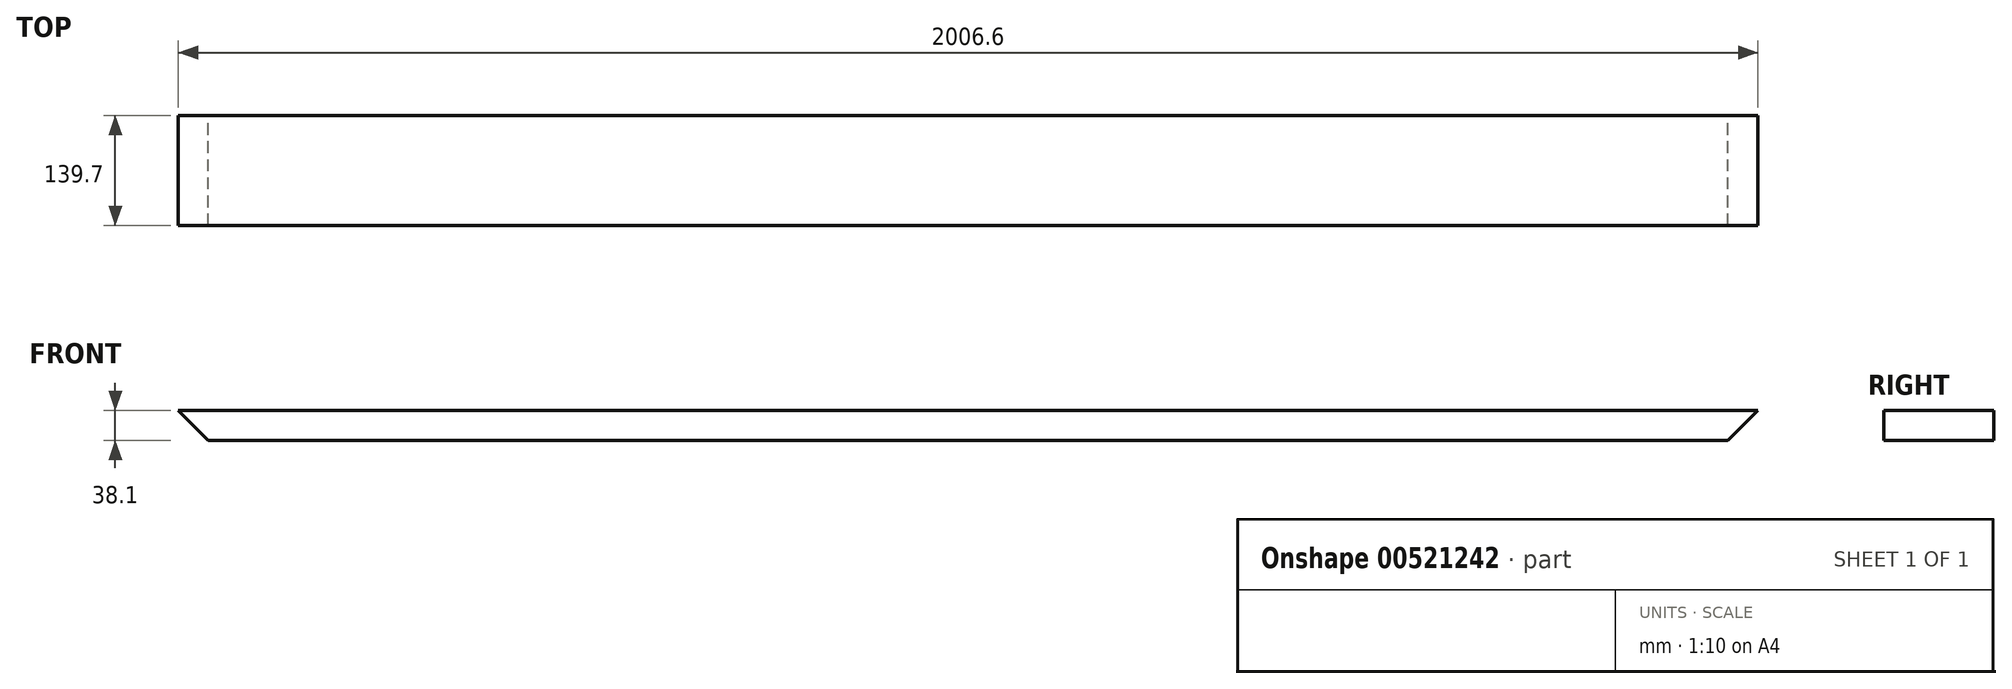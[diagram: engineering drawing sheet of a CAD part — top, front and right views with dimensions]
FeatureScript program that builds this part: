
annotation { "Feature Type Name" : "Feature", "Feature Type Description" : "" }
export const myFeature = defineFeature(function(context is Context, id is Id, definition is map)
    precondition{}
    {
        {
            var Q0;
            Q0=qCreatedBy(makeId("Front.planeOp"),FACE);
            var sketch = newSketch(context, id + "F0", { "sketchPlane" : qUnion([Q0])});
            skLineSegment(sketch, "E0", {"start": v(-965.2, 0) * mm, "end": v(-1003.3, 38.1) * mm});
            skLineSegment(sketch, "E1", {"start": v(-1003.3, 38.1) * mm, "end": v(1003.3, 38.1) * mm});
            skLineSegment(sketch, "E2", {"start": v(1003.3, 38.1) * mm, "end": v(965.2, 0) * mm});
            skLineSegment(sketch, "E3", {"start": v(965.2, 0) * mm, "end": v(-965.2, 0) * mm});
            skLineSegment(sketch, "E4", {"start": v(0, 570.25) * mm, "end": v(0, -656.25) * mm});
            skLineSegment(sketch, "E5", {"start": v(-542.33, 0) * mm, "end": v(651.2, 0) * mm});
            skSolve(sketch);
        }
        {
            var Q0;
            {var subQ0=sQuery(id+"F0.wireOp",EDGE,"E2");Q0=makeQuery(id+"F0.imprint","IMPRINT",FACE,{"disambiguationData":[TD([[makeQuery(id+"F0.imprint","IMPRINT",EDGE,{"derivedFrom":subQ0}),-1.0]])]});}
            var Q1;
            {var subQ0=sQuery(id+"F0.wireOp",EDGE,"E0");Q1=makeQuery(id+"F0.imprint","IMPRINT",FACE,{"disambiguationData":[TD([[makeQuery(id+"F0.imprint","IMPRINT",EDGE,{"derivedFrom":subQ0}),-1.0]])]});}
            extrude(context, id + "F1", {"entities" : qUnion([Q0, Q1]), "depth" : 139.7 * mm, "offsetDistance" : 25.4 * mm});
        }
    });
